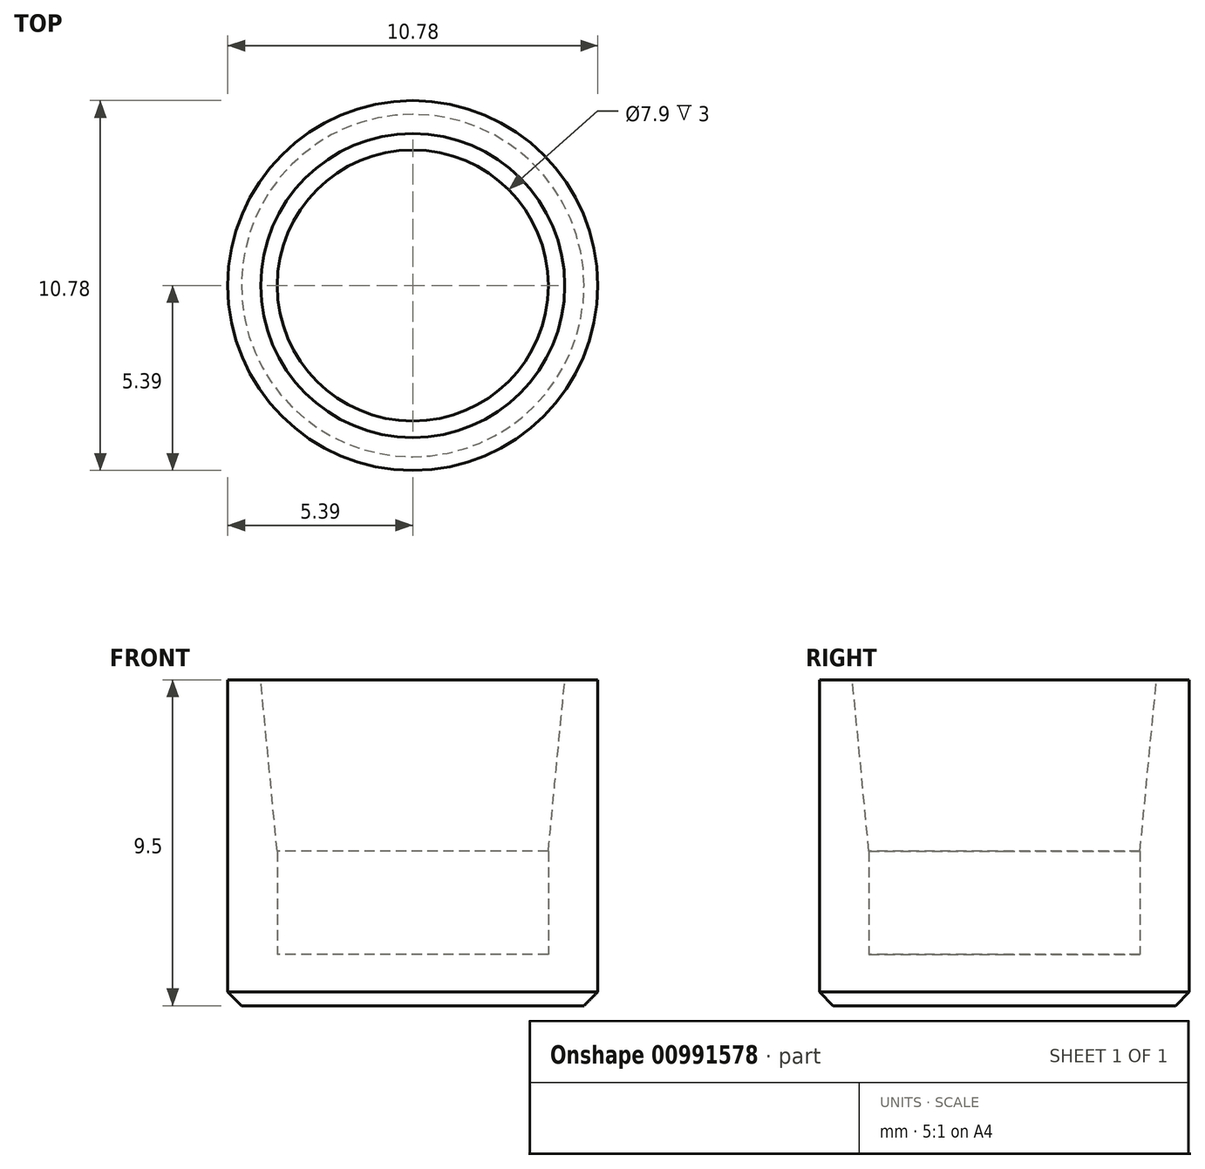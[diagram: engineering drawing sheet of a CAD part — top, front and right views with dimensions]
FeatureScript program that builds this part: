
annotation { "Feature Type Name" : "Feature", "Feature Type Description" : "" }
export const myFeature = defineFeature(function(context is Context, id is Id, definition is map)
    precondition{}
    {
        {
            var Q0;
            Q0=qCreatedBy(makeId("Top.planeOp"),FACE);
            var sketch = newSketch(context, id + "F0", { "sketchPlane" : qUnion([Q0])});
            skCircle(sketch, "E0", {"center": v(0, 0) * mm, "radius": 3.95 * mm});
            skCircle(sketch, "E1.0", {"center": v(0, 0) * mm, "radius": 5.4 * mm});
            skSolve(sketch);
        }
        {
            var Q0;
            Q0 = qSketchRegion(id + "F0", true);
            var Q1;
            Q1=makeQuery(id+"F0.imprint","IMPRINT",FACE,{"disambiguationData":[TD([[makeQuery(id+"F0.imprint","IMPRINT",EDGE,{"derivedFrom":sQuery(id+"F0.wireOp",EDGE,"E0")}),1.0]])]});
            extrude(context, id + "F1", {"entities" : qUnion([Q0, Q1]), "oppositeDirection" : true, "depth" : 1.5 * mm, "offsetDistance" : 25 * mm});
        }
        {
            var Q0;
            Q0=makeQuery(id+"F0.imprint","IMPRINT",FACE,{"disambiguationData":[TD([[makeQuery(id+"F0.imprint","IMPRINT",EDGE,{"derivedFrom":sQuery(id+"F0.wireOp",EDGE,"E0")}),-1.0]])]});
            extrude(context, id + "F2", {"entities" : qUnion([Q0]), "operationType" : NewBodyOperationType.ADD, "depth" : 8 * mm, "offsetDistance" : 25 * mm});
        }
        {
            var Q0;
            Q0=makeQuery(id+"F2.opExtrude","CAP_EDGE",EDGE,{"disambiguationData":[OSD([sQuery(id+"F0.wireOp",EDGE,"E0")])],"isStart":false});
            chamfer(context, id + "F3", {"entities" : qUnion([Q0]), "chamferType" : ChamferType.TWO_OFFSETS, "width1" : .48 * mm, "oppositeDirection" : true, "width2" : 5 * mm, "tangentPropagation" : true});
        }
        {
            var Q0;
            Q0=makeQuery(id+"F1.opExtrude","CAP_FACE",FACE,{"disambiguationData":[OSD([sQuery(id+"F0.wireOp",EDGE,"E1.0")])],"isStart":false});
            chamfer(context, id + "F4", {"entities" : qUnion([Q0]), "width" : .4 * mm, "tangentPropagation" : true});
        }
    });
